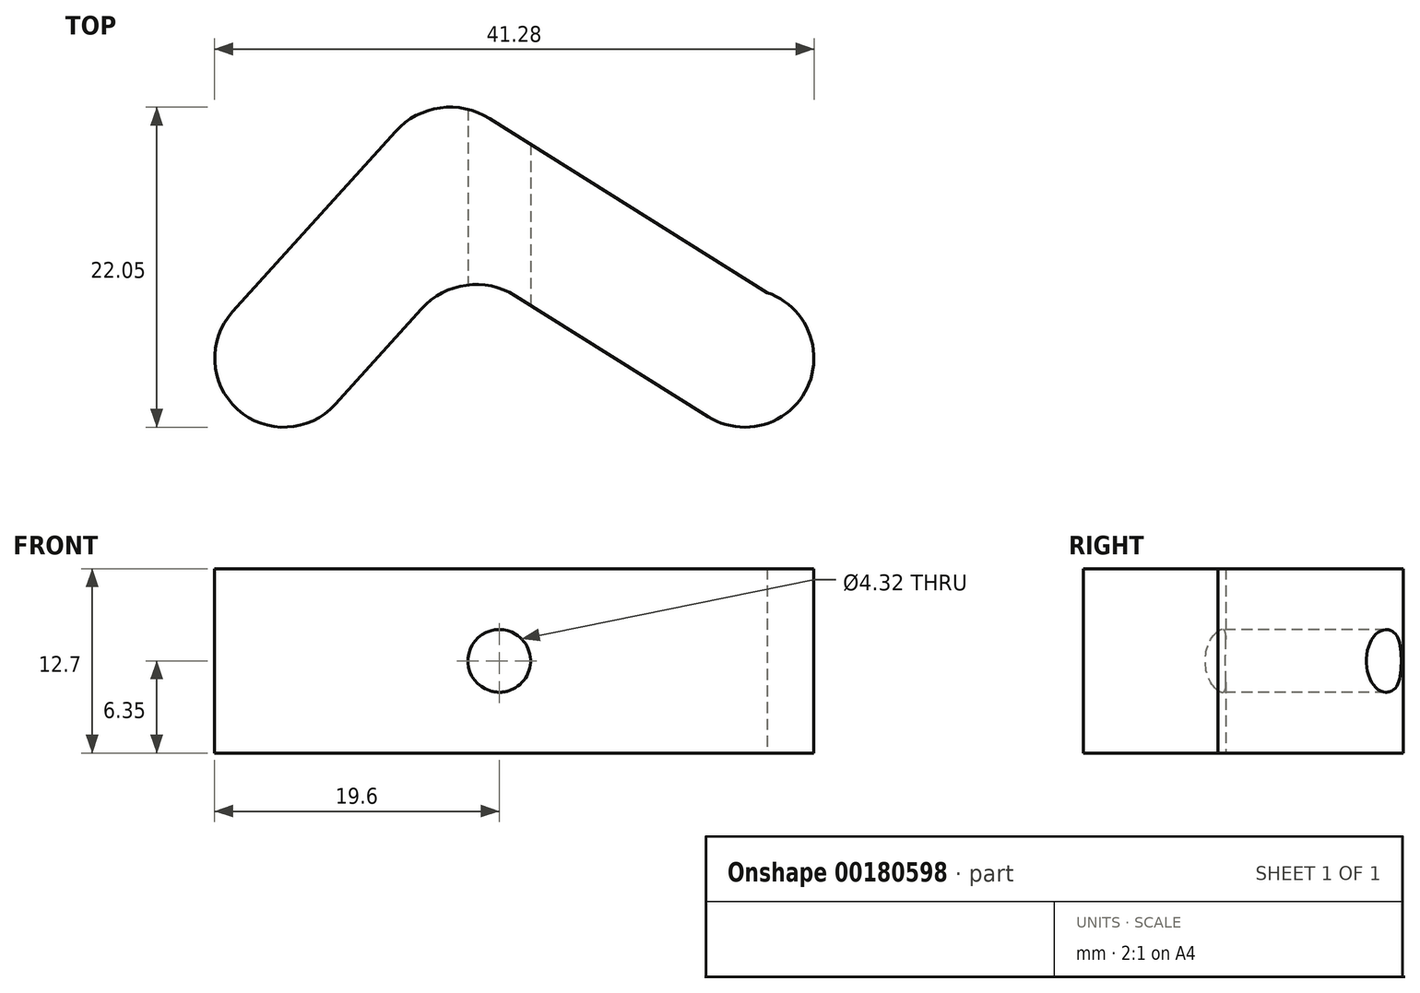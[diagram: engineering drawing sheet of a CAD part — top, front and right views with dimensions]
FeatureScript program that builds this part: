
annotation { "Feature Type Name" : "Feature", "Feature Type Description" : "" }
export const myFeature = defineFeature(function(context is Context, id is Id, definition is map)
    precondition{}
    {
        {
            var Q0;
            Q0=qCreatedBy(makeId("Top.planeOp"),FACE);
            var sketch = newSketch(context, id + "F0", { "sketchPlane" : qUnion([Q0])});
            skArc(sketch, "E0", {"start": v(-18.37, 3.2) * mm, "mid": v(-18.03, -3.53) * mm, "end": v(-11.3, -3.2) * mm});
            skArc(sketch, "E1", {"start": v(14.38, -4.03) * mm, "mid": v(21.21, -2.04) * mm, "end": v(18.44, 4.51) * mm});
            skLineSegment(sketch, "E2", {"start": v(-11.3, -3.2) * mm, "end": v(-2.5, 6.56) * mm});
            skLineSegment(sketch, "E3", {"start": v(14.38, -4.03) * mm, "end": v(-2.5, 6.56) * mm});
            skLineSegment(sketch, "E4", {"start": v(20.31, 3.34) * mm, "end": v(-4.28, 18.77) * mm});
            skLineSegment(sketch, "E5", {"start": v(-18.37, 3.2) * mm, "end": v(-4.28, 18.77) * mm});
            skSolve(sketch);
        }
        {
            var Q0;
            Q0 = qSketchRegion(id + "F0", true);
            extrude(context, id + "F1", {"entities" : qUnion([Q0]), "endBound" : BoundingType.SYMMETRIC, "depth" : 12.7 * mm});
        }
        {
            var Q0;
            Q0=makeQuery(id+"F1.opExtrude","SWEPT_EDGE",EDGE,{"disambiguationData":[OSD([sQuery(id+"F0.wireOp",EDGE,"E4"),sQuery(id+"F0.wireOp",EDGE,"E5")])]});
            var Q1;
            Q1=makeQuery(id+"F1.opExtrude","SWEPT_EDGE",EDGE,{"disambiguationData":[OSD([sQuery(id+"F0.wireOp",EDGE,"E2"),sQuery(id+"F0.wireOp",EDGE,"E3")])]});
            fillet(context, id + "F2", {"entities" : qUnion([Q0, Q1]), "radius" : 5.08 * mm, "tangentPropagation" : true, "allowEdgeOverflow" : false});
        }
        {
            var Q0;
            Q0=qCreatedBy(makeId("Front.planeOp"),FACE);
            var sketch = newSketch(context, id + "F3", { "sketchPlane" : qUnion([Q0])});
            skCircle(sketch, "E6", {"center": v(0, 0) * mm, "radius": 2.16 * mm});
            skSolve(sketch);
        }
        {
            var Q0;
            Q0 = qSketchRegion(id + "F3", true);
            extrude(context, id + "F4", {"entities" : qUnion([Q0]), "operationType" : NewBodyOperationType.REMOVE, "endBound" : BoundingType.THROUGH_ALL, "oppositeDirection" : true, "depth" : 25.4 * mm});
        }
    });
